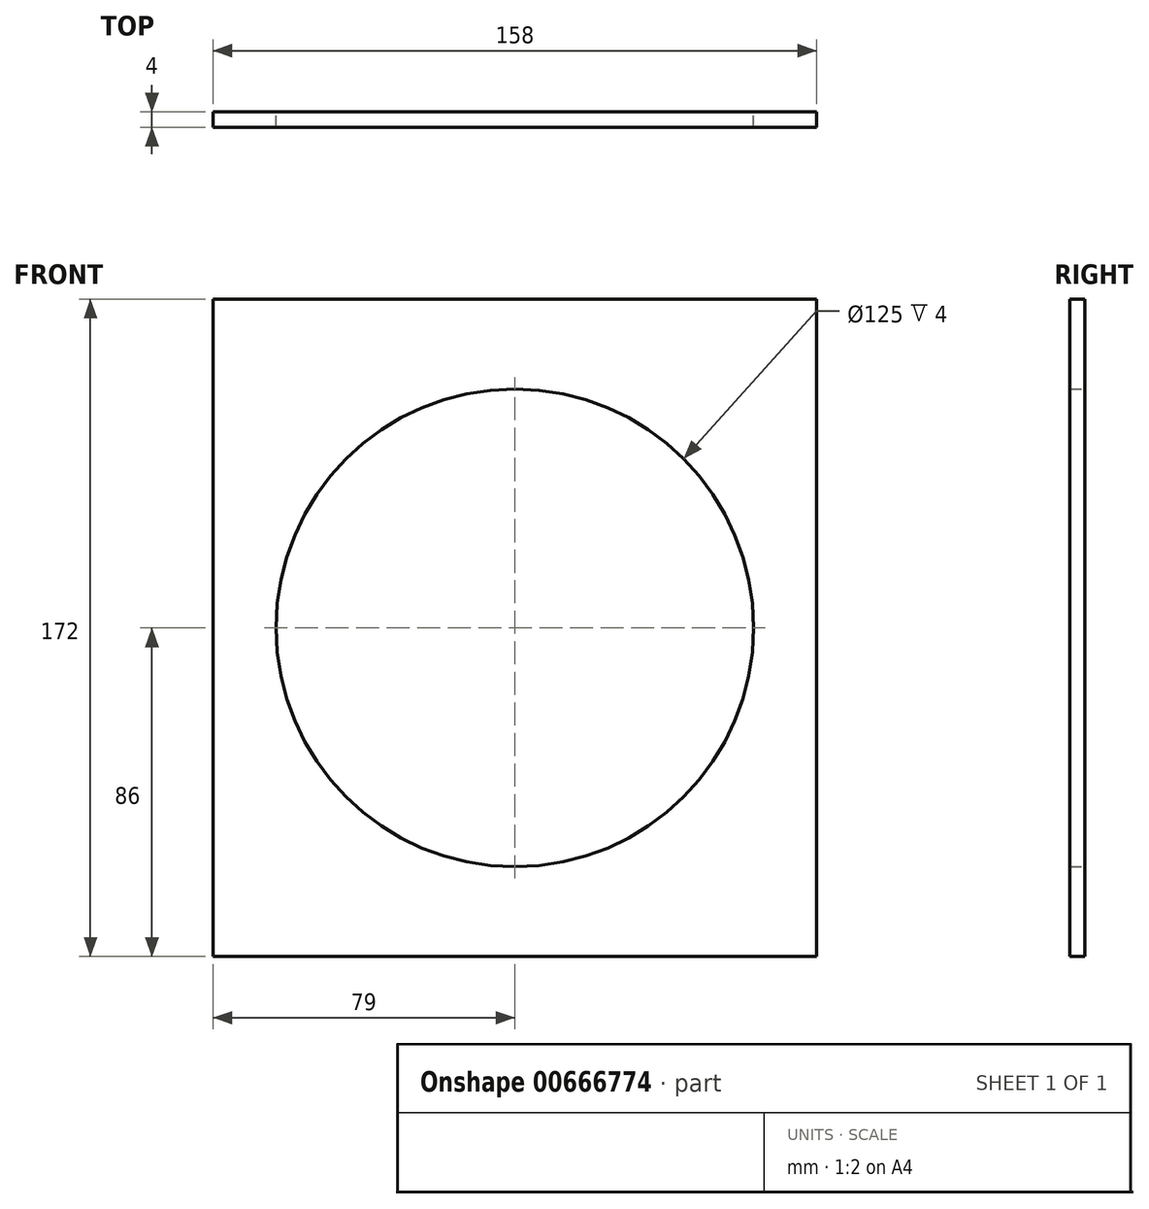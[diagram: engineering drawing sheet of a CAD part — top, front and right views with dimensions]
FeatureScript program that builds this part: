
annotation { "Feature Type Name" : "Feature", "Feature Type Description" : "" }
export const myFeature = defineFeature(function(context is Context, id is Id, definition is map)
    precondition{}
    {
        {
            var Q0;
            Q0=qCreatedBy(makeId("Front.planeOp"),FACE);
            var sketch = newSketch(context, id + "F0", { "sketchPlane" : qUnion([Q0])});
            skLineSegment(sketch, "E0.bottom", {"start": v(-79, 86) * mm, "end": v(79, 86) * mm});
            skLineSegment(sketch, "E0.top", {"start": v(-79, -86) * mm, "end": v(79, -86) * mm});
            skLineSegment(sketch, "E0.left", {"start": v(-79, 86) * mm, "end": v(-79, -86) * mm});
            skLineSegment(sketch, "E0.right", {"start": v(79, 86) * mm, "end": v(79, -86) * mm});
            skPoint(sketch, "E0.middle", {"position": v(0, 0) * mm});
            skCircle(sketch, "E1", {"center": v(0, 0) * mm, "radius": 88 * mm, "construction": true});
            skCircle(sketch, "E2", {"center": v(0, 0) * mm, "radius": 62.5 * mm});
            skSolve(sketch);
        }
        {
            var Q0;
            Q0 = qSketchRegion(id + "F0", true);
            extrude(context, id + "F1", {"entities" : qUnion([Q0]), "depth" : 4 * mm, "offsetDistance" : 25 * mm});
        }
    });
